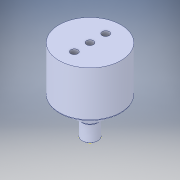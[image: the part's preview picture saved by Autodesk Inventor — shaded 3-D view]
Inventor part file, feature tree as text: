
AUTODESK INVENTOR PART (.ipt)
format: ipt  version: 2018 (Build 220112000, 112)  size: 299,520 bytes
history: native  units: in
note: dims shown in document units (in); Inventor stores cm internally (conversion verified against a paired STEP export)
features: sketch x11, extrude x11, fillet x4, other x4, projected_geometry x3, plane x2, loft x2, pattern_circular x1, chamfer x1
ambient origin geometry x8: Origin, YZ Plane, XZ Plane, XY Plane, X Axis, Y Axis, Z Axis, Center Point
bodies: Solid1 (feature_tree)
feature tree (39):
  plane  "Work Plane1"
  sketch  "Sketch1"  dims[d0=0.3937in d1=0.0in d2=1.75in d3=0.0in]
  extrude  "Extrusion1"  Depth=1.75in TaperAngle=0.0deg
  extrude  "Extrusion2"  Depth=1.0in
  sketch  "Sketch2"  dims[d25=0.45in d26=1.0in]
  extrude  "Extrusion3"  Depth=0.25in
  sketch  "Sketch10"  dims[d35=0.5in d36=0.0in d37=0.0in d38=90.0deg]
  extrude  "Extrusion4"  TaperAngle=0.0deg  [1 undecoded]
  loft  "Loft2"
  loft  "Loft3"
  extrude  "Extrusion5"  Depth=0.481in
  fillet  "Fillet1"  Radius=0.0787in
  extrude  "Extrusion6"  Depth=0.25in TaperAngle=0.0deg
  pattern_circular  "Circular Pattern1"  Count=6  [1 undecoded]
  extrude  "Extrusion7"  Depth=0.25in TaperAngle=0.0deg
  extrude  "Extrusion8"  Depth=1.0in
  fillet  "Fillet2"  Radius=0.25in
  plane  "Work Plane3"
  sketch  "Sketch18"  dims[d61=0.45in d62=1.0in d63=0.25in d64=0.0in]
  extrude  "Extrusion9"  Depth=0.45in
  extrude  "Extrusion10"  Depth=1.0in
  extrude  "Extrusion11"  Depth=0.25in TaperAngle=0.0deg
  chamfer  "Chamfer1"  Distance=0.25in
  fillet  "Fillet3"  Radius=0.25in
  sketch  "Sketch9"  dims[d27=0.625in d28=0.0in d34=0.25in]
  projected_geometry  "Projected Loop7"
  projected_geometry  "Projected Loop8"
  sketch  "Sketch12"  dims[d39=0.0in d40=90.0deg d41=0.0in d42=90.0deg]
  other  "Edges2"
  other  "Edges3"
  other  "Edges4"
  other  "Edges5"
  sketch  "Sketch13"  dims[d43=0.0in d44=90.0deg d45=0.25in d46=0.0in]
  sketch  "Sketch14"  dims[d47=0.125in d49=0.481in d50=0.0787in]
  sketch  "Sketch16"  dims[d51=0.0394in d52=0.25in d53=0.0in d54=2.3622in d55=2.4737in]
  sketch  "Sketch17"  dims[d58=0.0591in d59=0.25in d60=0.0in]
  projected_geometry  "Projected Loop10"
  sketch  "Sketch19"  dims[d65=0.25in d66=0.45in d67=1.0in d68=0.25in d69=0.0in d70=0.25in d71=0.0in d72=0.25in d73=0.0in d74=0.0625in d75=0.0787in d76=45.0deg d77=0.0625in]
  fillet  "Fillet10"  Radius=0.0625in
note: 2 required parameter values undecoded (feature->parameter linkage not recoverable at this tier; creation-order binding heuristic only, values carry confidence <= 0.55)
